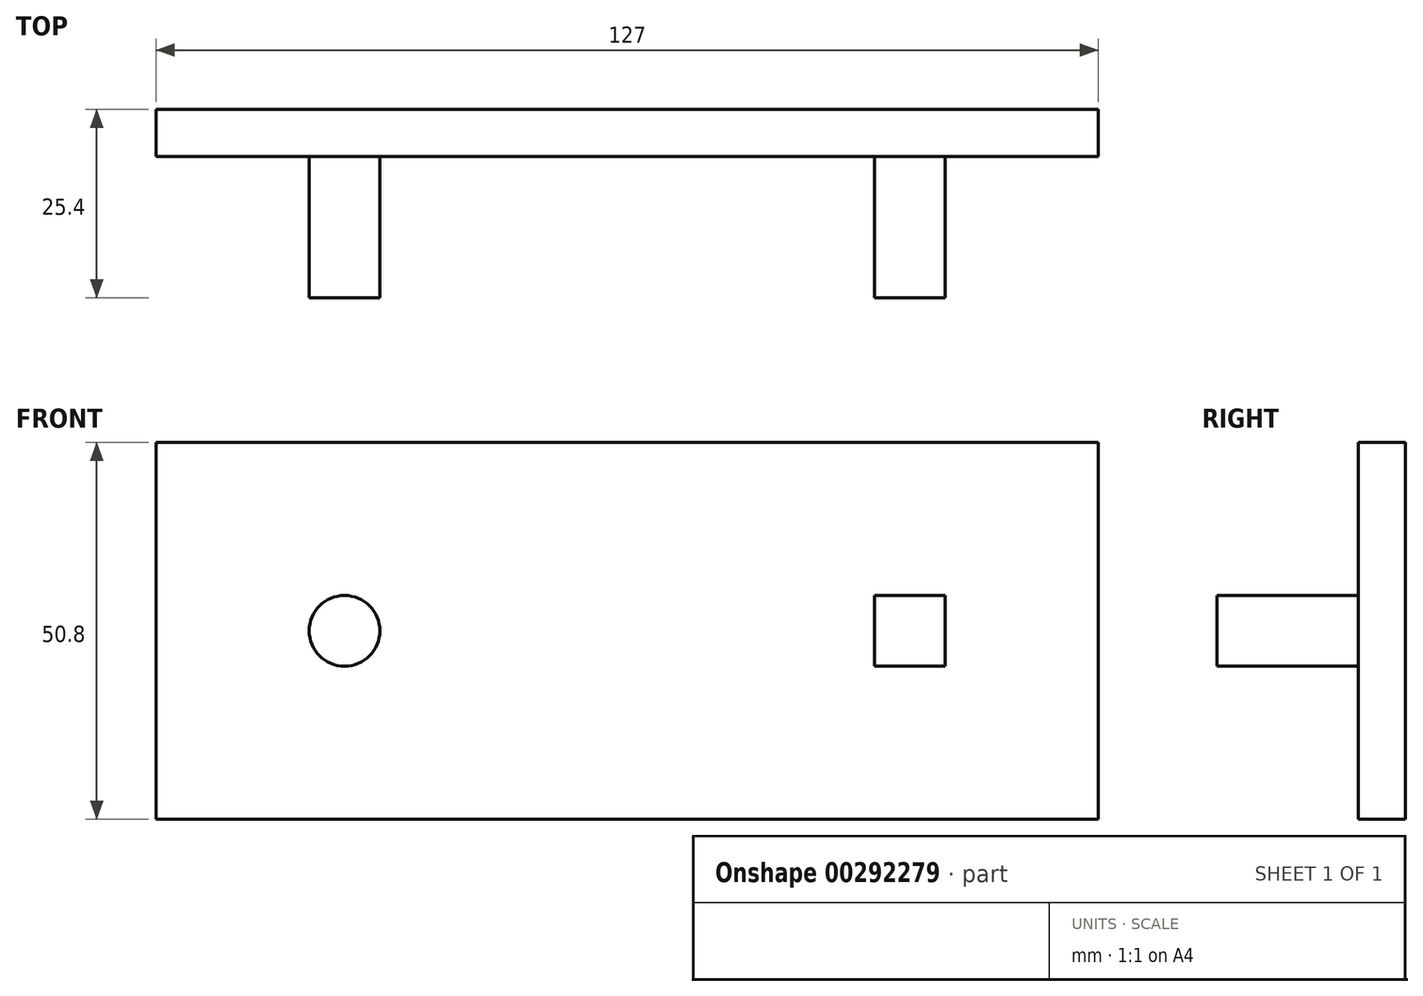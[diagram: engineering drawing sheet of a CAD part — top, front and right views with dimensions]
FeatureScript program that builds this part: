
annotation { "Feature Type Name" : "Feature", "Feature Type Description" : "" }
export const myFeature = defineFeature(function(context is Context, id is Id, definition is map)
    precondition{}
    {
        {
            var Q0;
            Q0=qCreatedBy(makeId("Front.planeOp"),FACE);
            var sketch = newSketch(context, id + "F0", { "sketchPlane" : qUnion([Q0])});
            skLineSegment(sketch, "E0", {"start": v(0, 0) * mm, "end": v(0, 50.8) * mm});
            skLineSegment(sketch, "E1", {"start": v(0, 0) * mm, "end": v(127, 0) * mm});
            skLineSegment(sketch, "E2", {"start": v(0, 50.8) * mm, "end": v(127, 50.8) * mm});
            skLineSegment(sketch, "E3", {"start": v(127, 50.8) * mm, "end": v(127, 0) * mm});
            skSolve(sketch);
        }
        {
            var Q0;
            Q0=makeQuery(id+"F0.imprint","IMPRINT",FACE,{"disambiguationData":[TD([[makeQuery(id+"F0.imprint","IMPRINT",EDGE,{"derivedFrom":sQuery(id+"F0.wireOp",EDGE,"E0")}),-1.0]])]});
            extrude(context, id + "F1", {"entities" : qUnion([Q0]), "depth" : 6.35 * mm});
        }
        {
            var Q0;
            Q0=makeQuery(id+"F1.opExtrude","CAP_FACE",FACE,{"disambiguationData":[OSD([sQuery(id+"F0.wireOp",EDGE,"E0"),sQuery(id+"F0.wireOp",EDGE,"E1"),sQuery(id+"F0.wireOp",EDGE,"E2"),sQuery(id+"F0.wireOp",EDGE,"E3")])],"isStart":false});
            var sketch = newSketch(context, id + "F2", { "sketchPlane" : qUnion([Q0])});
            skLineSegment(sketch, "E4", {"start": v(127, 0) * mm, "end": v(127, 25.4) * mm});
            skLineSegment(sketch, "E5", {"start": v(106.36, 30.16) * mm, "end": v(106.36, 20.64) * mm});
            skLineSegment(sketch, "E6", {"start": v(106.36, 20.64) * mm, "end": v(96.84, 20.64) * mm});
            skLineSegment(sketch, "E7", {"start": v(96.84, 20.64) * mm, "end": v(96.84, 30.16) * mm});
            skLineSegment(sketch, "E8", {"start": v(96.84, 30.16) * mm, "end": v(106.36, 30.16) * mm});
            skCircle(sketch, "E9", {"center": v(25.4, 25.4) * mm, "radius": 4.76 * mm});
            skSolve(sketch);
        }
        {
            var Q0;
            Q0=makeQuery(id+"F2.imprint","IMPRINT",FACE,{"disambiguationData":[TD([[makeQuery(id+"F2.imprint","IMPRINT",EDGE,{"derivedFrom":sQuery(id+"F2.wireOp",EDGE,"E5")}),-1.0]])]});
            var Q1;
            Q1=makeQuery(id+"F2.imprint","IMPRINT",FACE,{"disambiguationData":[TD([[makeQuery(id+"F2.imprint","IMPRINT",EDGE,{"derivedFrom":sQuery(id+"F2.wireOp",EDGE,"E9")}),1.0]])]});
            extrude(context, id + "F3", {"entities" : qUnion([Q0, Q1]), "operationType" : NewBodyOperationType.ADD, "depth" : 19.05 * mm});
        }
    });
